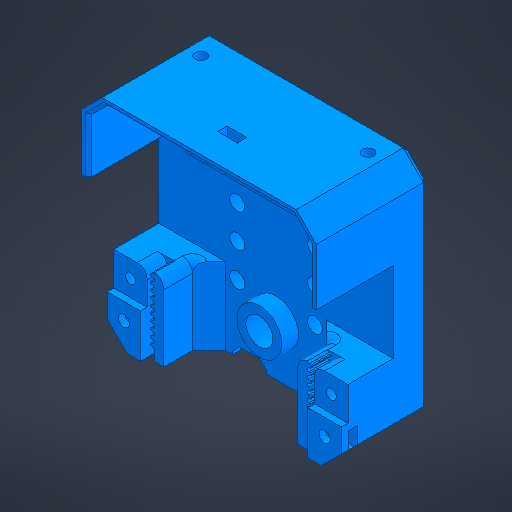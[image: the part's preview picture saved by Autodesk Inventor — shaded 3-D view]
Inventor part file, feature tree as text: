
AUTODESK INVENTOR PART (.ipt)
format: ipt  version: 2025.1 (Build 291241000, 241)  size: 1,436,672 bytes
history: native  units: mm
features: extrude x15, sketch x9, chamfer x6, projected_geometry x5, mirror x3, fillet x3, plane x2
ambient origin geometry x8: Origin, YZ Plane, XZ Plane, XY Plane, X Axis, Y Axis, Z Axis, Center Point
bodies: Solid1 (feature_tree)
feature tree (43):
  sketch  "Sketch1"  dims[d19=5.4mm d20=5.4mm]
  extrude  "Extrusion1"  Depth=5.4mm
  extrude  "Extrusion2"  Depth=4.0mm
  extrude  "Extrusion11"  Depth=4.0mm
  plane  "Work Plane1"
  extrude  "Extrusion9"  Depth=34.0mm
  extrude  "Extrusion10"  Depth=24.0mm
  extrude  "Extrusion13"  Depth=70.0mm
  mirror  "Mirror2"
  fillet  "Fillet5"  Radius=70.0mm
  chamfer  "Chamfer4"  Distance=11.0mm
  extrude  "Extrusion16"  Depth=5.0mm
  extrude  "Extrusion17"  Depth=6.0mm
  extrude  "Extrusion18"  Depth=10.0mm
  fillet  "Fillet6"  Radius=10.0mm
  chamfer  "Chamfer5"  Distance=8.0mm
  chamfer  "Chamfer7"  Distance=6.0mm
  chamfer  "Chamfer8"  Distance=6.0mm
  extrude  "Extrusion20"  Depth=5.0mm TaperAngle=0.0deg
  fillet  "Fillet7"  Radius=12.0mm
  extrude  "Extrusion21"  TaperAngle=45.0deg  [1 undecoded]
  mirror  "Mirror3"
  extrude  "Extrusion22"  TaperAngle=45.0deg  [1 undecoded]
  extrude  "Extrusion23"  Depth=7.25mm
  chamfer  "Chamfer9"  Distance=3.0mm
  sketch  "Sketch9"  dims[d124=6.0mm d125=6.0mm]
  extrude  "Extrusion24"  Depth=7.25mm
  chamfer  "Chamfer10"  Distance=5.0mm
  mirror  "Mirror4"
  extrude  "Extrusion26"  Depth=10.0mm
  sketch  "Sketch Rectangular Pattern1"  dims[d21=5.4mm d22=4.0mm]
  plane  "Work Plane4"
  sketch  "Sketch4"  dims[d23=4.0mm d24=4.0mm]
  sketch  "Sketch5"  dims[d25=40.0mm d26=34.0mm]
  sketch  "Sketch6"  dims[d27=24.0mm d28=24.0mm]
  sketch  "Sketch7"  dims[d29=24.0mm d43=70.0mm d44=70.0mm d45=11.0mm d46=0.0mm]
  projected_geometry  "Projected Loop2"
  projected_geometry  "Projected Loop3"
  sketch  "Sketch8"  dims[d47=5.0mm d48=0.0mm d123=6.0mm]
  sketch  "Sketch10"  dims[d126=6.0mm d132=100.0mm d134=10.0mm d136=1.1mm d137=2.0mm d138=0.25mm d139=-0.75mm d140=1.15mm d141=1.0mm d142=2.0mm d143=3.4mm d144=3.0mm d145=5.0mm d146=10.0mm d147=10.0mm d149=5.0mm d150=10.0mm d151=8.0mm d152=6.0mm d153=0.0mm d154=6.0mm d155=0.0mm d156=5.0mm d157=0.0mm d158=12.0mm d160=45.0deg d161=45.0deg d162=6.0mm d164=3.0mm d165=3.4mm d166=5.0mm d169=10.0mm d170=9.0mm d171=9.0mm d172=9.0mm d174=11.0mm d175=2.0mm d176=0.0mm d177=2.0mm d178=4.0mm d179=45.0deg d187=9.0mm d188=9.0mm d189=9.0mm d190=6.0mm d191=0.0mm d192=16.5mm d193=0.0mm d194=2.0mm d195=2.0mm d196=2.0mm d197=2.0mm d198=2.0mm d199=2.0mm d200=12.0mm d201=12.0mm d202=23.0mm d203=0.0mm d204=3.0mm d205=10.0mm d206=6.0mm d207=45.0deg d209=7.0mm d210=2.0mm d216=5.0mm d217=2.0mm d218=45.0deg d219=1.0mm d220=2.0mm d221=45.0deg d223=3.4mm d224=50.0mm d225=13.0mm d226=10.0mm d227=0.0mm d228=3.0mm d229=5.9mm d230=2.0mm d231=2.8mm d232=7.7mm d233=0.0mm d234=5.9mm d235=2.8mm d237=7.9mm d238=0.0mm d239=2.0mm d241=3.0mm d242=0.0mm d243=10.0mm d244=2.0mm d245=2.0mm d246=2.0mm d247=45.0deg d253=4.5mm d254=4.5mm d256=5.6mm d257=5.6mm d262=0.0mm d263=0.0mm d278=10.0mm d279=4.5mm d280=4.5mm d281=5.6mm d282=5.6mm d283=10.0mm d284=4.5mm d285=4.5mm d286=5.6mm d287=5.6mm d289=3.0mm d290=5.6mm d292=23.2mm d293=30.0mm d294=2.0mm d295=2.0mm d296=45.0deg d297=8.1mm d298=7.25mm d299=0.0mm d211=0.5mm d212=0.872665mm]
  projected_geometry  "Projected Loop4"
  projected_geometry  "Projected Loop5"
  projected_geometry  "Projected Loop6"
note: 2 required parameter values undecoded (feature->parameter linkage not recoverable at this tier; creation-order binding heuristic only, values carry confidence <= 0.55)
